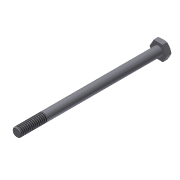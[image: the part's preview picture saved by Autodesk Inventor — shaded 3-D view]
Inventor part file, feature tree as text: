
AUTODESK INVENTOR PART (.ipt)
format: ipt  version: 2011 SP1 (Build 150282100, 282)  size: 156,160 bytes
history: native  units: in
note: dims shown in document units (in); Inventor stores cm internally (conversion verified against a paired STEP export)
features: sketch x3, extrude x2, projected_geometry x2, thread x1, chamfer x1, revolve x1, fillet x1
ambient origin geometry x8: Origin, YZ Plane, XZ Plane, XY Plane, X Axis, Y Axis, Z Axis, Center Point
bodies: Solid1 (feature_tree)
feature tree (11):
  extrude  "Extrusion1"  Depth=4.0in TaperAngle=0.0deg
  extrude  "Extrusion2"  Depth=0.1562in TaperAngle=0.0deg
  thread  "Thread1"  [1 undecoded]
  chamfer  "Chamfer1"  Distance=0.02in Angle=45.0deg
  revolve  "Revolution1"  [1 undecoded]
  fillet  "Fillet1"  [1 undecoded]
  sketch  "Sketch1"  dims[d0=0.25in d1=4.0in d2=0.0in]
  sketch  "Sketch2"  dims[d3=0.4375in d4=0.1562in d5=0.0in d6=0.75in d7=0.0in d8=0.02in d9=0.125in d10=45.0deg]
  sketch  "Sketch3"  dims[d11=90.0deg d12=0.01in]
  projected_geometry  "Projected Loop1"
  projected_geometry  "Projected Loop2"
note: 3 required parameter values undecoded (feature->parameter linkage not recoverable at this tier; creation-order binding heuristic only, values carry confidence <= 0.55)